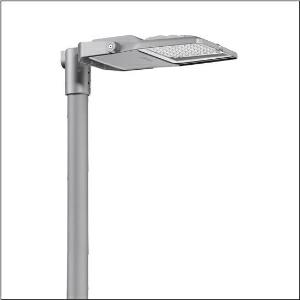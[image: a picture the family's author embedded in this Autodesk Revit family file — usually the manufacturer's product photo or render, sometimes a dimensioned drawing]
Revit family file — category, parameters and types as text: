
# Revit family: floodlight_fl_21_mini___pl64_5xa7776c2e3a_3ffb
name_source: partatom
category: Lighting Fixtures
units: mm (PartAtom-declared; Revit-internal decimal feet)

## family parameters
Cut with Voids When Loaded = No
Host = Face
Light Source = No
Part Type = Normal
Room Calculation Point = No
Round Connector Dimension = Use Diameter
Shared = No

## types (1)
- --- (1 x LED, 11770 lm, 89 W, 3000K)
    Apparent Load = 89 VA
    CIE Flux Codes = 28 80 98 100 100
    Color Rendering = 70
    Color Temperature = 3000K
    Default Elevation = 1800 mm
    Description = Floodlight FL 21 mini, floodlight, primary light control with lens, of PMMA, primary optical cover: protective disc, of toughened safety glass, transparent, light distribution: PL64, light emission: direct distribution, installation type: surface-mounted, LED, High Power LED, rated luminous flux: 11.770lm, luminous efficacy: 132lm/W, light colour: 730, colour temperature: 3000K, control: flexible luminous flux parameterisation, time-dependent luminous flux control, constant luminous flux control, overheat protection, pre-setting: logarithmic dimming characteristic, with terminal, 6-pole, mains connection: 220..240V, AC, 50/60Hz, start of lifetime: 89W, end of service life: 94W, reduction: 43W, luminaire housing, of diecast aluminium, powder-coated, Siteco® metallic grey (DB 702S), corrosivity category C5 mid according to DIN EN ISO 12944, sealing non-destructively replaceable, please order mast flange separately, mast bracket, of steel, galvanised, powder-coated, Siteco® metallic grey (DB 702S), Smart Interface below and above, protection rating (complete): IP66, insulation class (complete): insulation class II (safety insulation), certification: CE, ENEC, VDE, protection symbol: D, impact resistance: IK08, permissible operating ambient temperature: -40..+40°C, permissible operating ambient temperature for outdoor applications: -40..+50°C, standard: DIN EN 12944, LABS conformity tested according to VDMA 24364:2018-05, packaging unit: 1 piece

Light Distribution: PL64
    Height = 70 mm
    Lamp = 1 x LED
    Lamp Light Flux = 11770 lm
    Lamp Power = 89 W
    Lamp count = 1
    Length = 485 mm
    Luminous efficacy = 132 lm/W
    Manufacturer = Siteco
    ModVariant = No
    Model = 5XA7776C2E3A
    Number of Poles = 1
    OnlyDefault = Yes
    Power Factor = 1
    Product Name = Floodlight FL 21 mini | PL64
    Product group = floodlight | pylon annexe
    ProductGroupID = 6200
    Protection Class = Protection class II
    Protection Degree = IP 66
    RLX_Detail_Level = 1
    RLX_Emergency_Light_Flux = 0 lm
    RLX_Emergency_Type = 0
    RLX_Emergency_Type_DB = No
    RlxData = <blob elided: 100877 chars, md5=53274992>
    Socket = socket
    Standby Power = 0 W
    System Light Flux = 11770 lm
    System Power = 89 W
    Type Comments = factory setting: luminous flux: 100 % | dim-lin: 254 | 456 mA
    Type Image = l_1007125.jpg
    URL = http://relux.com
    VarID = @adj_135681
    Voltage = 0 V
    Weight = 0.00 kg
    Width = 337 mm

## geometry (parser evidence)
native form markers: Blend x4, Sweep x11
no freeform markers — native parametric forms only
